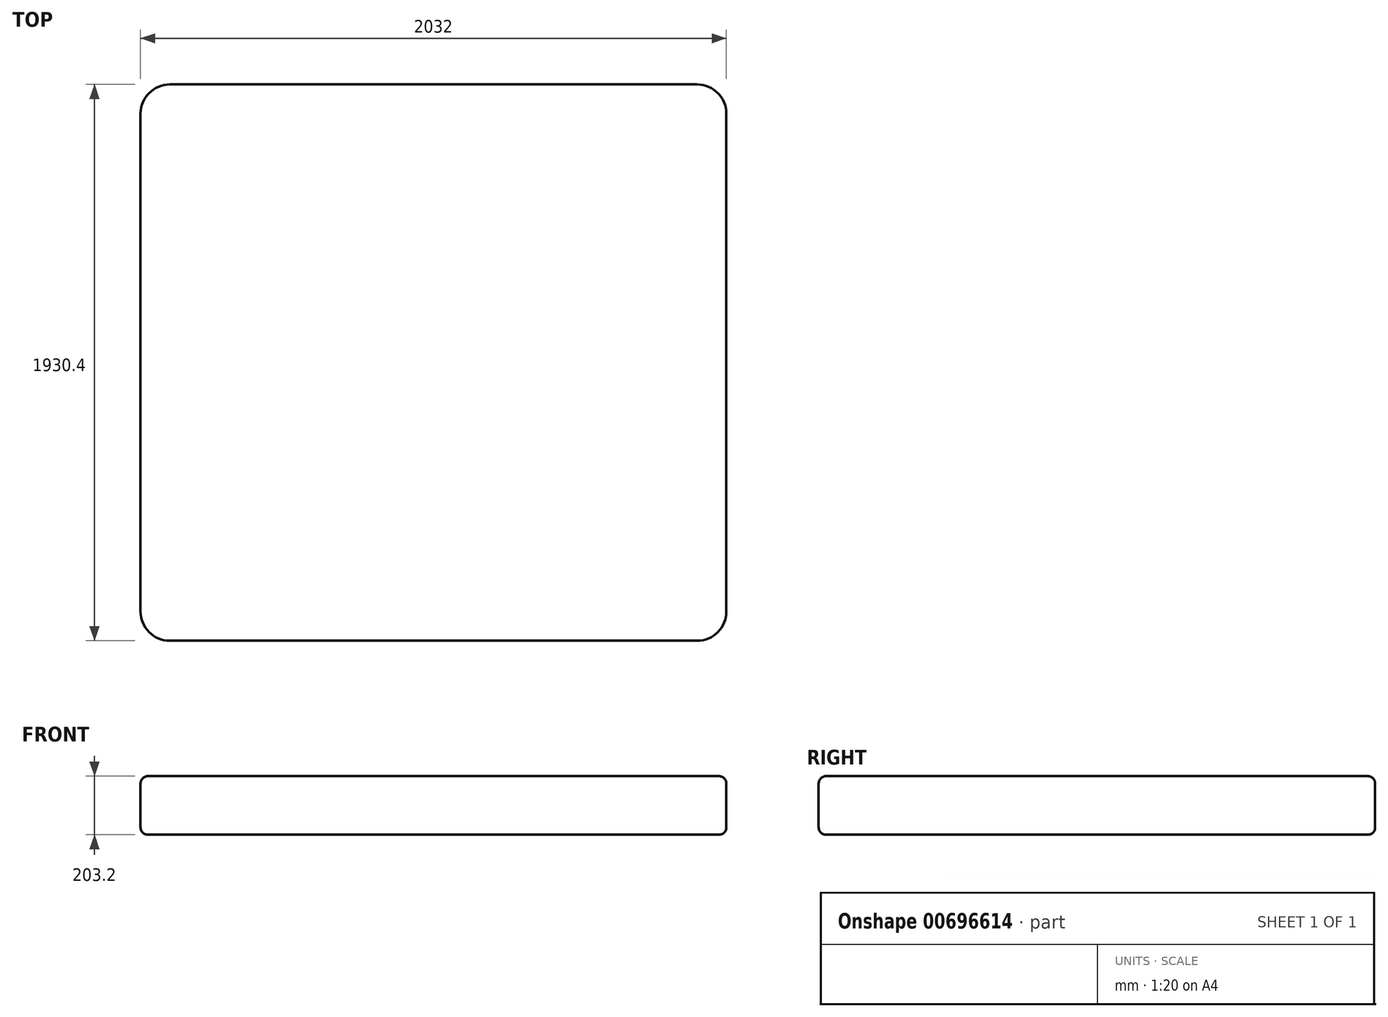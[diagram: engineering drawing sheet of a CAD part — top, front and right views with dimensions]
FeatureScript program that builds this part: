
annotation { "Feature Type Name" : "Feature", "Feature Type Description" : "" }
export const myFeature = defineFeature(function(context is Context, id is Id, definition is map)
    precondition{}
    {
        {
            var Q0;
            Q0=qCreatedBy(makeId("Top.planeOp"),FACE);
            var sketch = newSketch(context, id + "F0", { "sketchPlane" : qUnion([Q0])});
            skLineSegment(sketch, "E0.bottom", {"start": v(0, 0) * mm, "end": v(2032, 0) * mm});
            skLineSegment(sketch, "E0.top", {"start": v(0, 1930.4) * mm, "end": v(2032, 1930.4) * mm});
            skLineSegment(sketch, "E0.left", {"start": v(0, 0) * mm, "end": v(0, 1930.4) * mm});
            skLineSegment(sketch, "E0.right", {"start": v(2032, 0) * mm, "end": v(2032, 1930.4) * mm});
            skSolve(sketch);
        }
        {
            var Q0;
            Q0 = qSketchRegion(id + "F0", true);
            extrude(context, id + "F1", {"entities" : qUnion([Q0]), "depth" : 203.2 * mm, "offsetDistance" : 25.4 * mm});
        }
        {
            var Q0;
            Q0=makeQuery(id+"F1.opExtrude","SWEPT_EDGE",EDGE,{"disambiguationData":[OSD([sQuery(id+"F0.wireOp",EDGE,"E0.top"),sQuery(id+"F0.wireOp",EDGE,"E0.left")])]});
            var Q1;
            Q1=makeQuery(id+"F1.opExtrude","SWEPT_EDGE",EDGE,{"disambiguationData":[OSD([sQuery(id+"F0.wireOp",EDGE,"E0.bottom"),sQuery(id+"F0.wireOp",EDGE,"E0.left")])]});
            var Q2;
            Q2=makeQuery(id+"F1.opExtrude","SWEPT_EDGE",EDGE,{"disambiguationData":[OSD([sQuery(id+"F0.wireOp",EDGE,"E0.bottom"),sQuery(id+"F0.wireOp",EDGE,"E0.right")])]});
            var Q3;
            Q3=makeQuery(id+"F1.opExtrude","SWEPT_EDGE",EDGE,{"disambiguationData":[OSD([sQuery(id+"F0.wireOp",EDGE,"E0.top"),sQuery(id+"F0.wireOp",EDGE,"E0.right")])]});
            fillet(context, id + "F2", {"entities" : qUnion([Q0, Q1, Q2, Q3]), "radius" : 101.6 * mm, "tangentPropagation" : true, "allowEdgeOverflow" : false});
        }
        {
            var Q0;
            Q0=makeQuery(id+"F1.opExtrude","CAP_EDGE",EDGE,{"disambiguationData":[OSD([sQuery(id+"F0.wireOp",EDGE,"E0.top")])],"isStart":false});
            var Q1;
            {var subQ0=sQuery(id+"F0.wireOp",EDGE,"E0.left");var subQ1=sQuery(id+"F0.wireOp",EDGE,"E0.top");Q1=makeQuery(id+"F2.opFillet","BLEND_EDGE",EDGE,{"blendedFrom":[makeQuery(id+"F1.opExtrude","SWEPT_EDGE",EDGE,{"disambiguationData":[OSD([subQ1,subQ0])]}),makeQuery(id+"F1.opExtrude","CAP_FACE",FACE,{"disambiguationData":[OSD([sQuery(id+"F0.wireOp",EDGE,"E0.bottom"),subQ1,subQ0,sQuery(id+"F0.wireOp",EDGE,"E0.right")])],"isStart":false})],"blendedInto":[makeQuery(id+"F1.opExtrude","CAP_FACE",FACE,{"disambiguationData":[OSD([sQuery(id+"F0.wireOp",EDGE,"E0.bottom"),subQ1,subQ0,sQuery(id+"F0.wireOp",EDGE,"E0.right")])],"isStart":false})]});}
            var Q2;
            Q2=makeQuery(id+"F1.opExtrude","CAP_EDGE",EDGE,{"disambiguationData":[OSD([sQuery(id+"F0.wireOp",EDGE,"E0.left")])],"isStart":false});
            var Q3;
            {var subQ0=sQuery(id+"F0.wireOp",EDGE,"E0.left");var subQ1=sQuery(id+"F0.wireOp",EDGE,"E0.bottom");Q3=makeQuery(id+"F2.opFillet","BLEND_EDGE",EDGE,{"blendedFrom":[makeQuery(id+"F1.opExtrude","SWEPT_EDGE",EDGE,{"disambiguationData":[OSD([subQ1,subQ0])]}),makeQuery(id+"F1.opExtrude","CAP_FACE",FACE,{"disambiguationData":[OSD([subQ1,sQuery(id+"F0.wireOp",EDGE,"E0.top"),subQ0,sQuery(id+"F0.wireOp",EDGE,"E0.right")])],"isStart":false})],"blendedInto":[makeQuery(id+"F1.opExtrude","CAP_FACE",FACE,{"disambiguationData":[OSD([subQ1,sQuery(id+"F0.wireOp",EDGE,"E0.top"),subQ0,sQuery(id+"F0.wireOp",EDGE,"E0.right")])],"isStart":false})]});}
            var Q4;
            Q4=makeQuery(id+"F1.opExtrude","CAP_EDGE",EDGE,{"disambiguationData":[OSD([sQuery(id+"F0.wireOp",EDGE,"E0.bottom")])],"isStart":false});
            var Q5;
            {var subQ0=sQuery(id+"F0.wireOp",EDGE,"E0.right");var subQ1=sQuery(id+"F0.wireOp",EDGE,"E0.bottom");Q5=makeQuery(id+"F2.opFillet","BLEND_EDGE",EDGE,{"blendedFrom":[makeQuery(id+"F1.opExtrude","SWEPT_EDGE",EDGE,{"disambiguationData":[OSD([subQ1,subQ0])]}),makeQuery(id+"F1.opExtrude","CAP_FACE",FACE,{"disambiguationData":[OSD([subQ1,sQuery(id+"F0.wireOp",EDGE,"E0.top"),sQuery(id+"F0.wireOp",EDGE,"E0.left"),subQ0])],"isStart":false})],"blendedInto":[makeQuery(id+"F1.opExtrude","CAP_FACE",FACE,{"disambiguationData":[OSD([subQ1,sQuery(id+"F0.wireOp",EDGE,"E0.top"),sQuery(id+"F0.wireOp",EDGE,"E0.left"),subQ0])],"isStart":false})]});}
            var Q6;
            Q6=makeQuery(id+"F1.opExtrude","CAP_EDGE",EDGE,{"disambiguationData":[OSD([sQuery(id+"F0.wireOp",EDGE,"E0.right")])],"isStart":false});
            var Q7;
            {var subQ0=sQuery(id+"F0.wireOp",EDGE,"E0.right");var subQ1=sQuery(id+"F0.wireOp",EDGE,"E0.top");Q7=makeQuery(id+"F2.opFillet","BLEND_EDGE",EDGE,{"blendedFrom":[makeQuery(id+"F1.opExtrude","SWEPT_EDGE",EDGE,{"disambiguationData":[OSD([subQ1,subQ0])]}),makeQuery(id+"F1.opExtrude","CAP_FACE",FACE,{"disambiguationData":[OSD([sQuery(id+"F0.wireOp",EDGE,"E0.bottom"),subQ1,sQuery(id+"F0.wireOp",EDGE,"E0.left"),subQ0])],"isStart":false})],"blendedInto":[makeQuery(id+"F1.opExtrude","CAP_FACE",FACE,{"disambiguationData":[OSD([sQuery(id+"F0.wireOp",EDGE,"E0.bottom"),subQ1,sQuery(id+"F0.wireOp",EDGE,"E0.left"),subQ0])],"isStart":false})]});}
            fillet(context, id + "F3", {"entities" : qUnion([Q0, Q1, Q2, Q3, Q4, Q5, Q6, Q7]), "radius" : 25.4 * mm, "tangentPropagation" : true, "allowEdgeOverflow" : false});
        }
        {
            var Q0;
            {var subQ0=sQuery(id+"F0.wireOp",EDGE,"E0.right");var subQ1=sQuery(id+"F0.wireOp",EDGE,"E0.bottom");Q0=makeQuery(id+"F2.opFillet","BLEND_EDGE",EDGE,{"blendedFrom":[makeQuery(id+"F1.opExtrude","SWEPT_EDGE",EDGE,{"disambiguationData":[OSD([subQ1,subQ0])]}),makeQuery(id+"F1.opExtrude","CAP_FACE",FACE,{"disambiguationData":[OSD([subQ1,sQuery(id+"F0.wireOp",EDGE,"E0.top"),sQuery(id+"F0.wireOp",EDGE,"E0.left"),subQ0])],"isStart":true})],"blendedInto":[makeQuery(id+"F1.opExtrude","CAP_FACE",FACE,{"disambiguationData":[OSD([subQ1,sQuery(id+"F0.wireOp",EDGE,"E0.top"),sQuery(id+"F0.wireOp",EDGE,"E0.left"),subQ0])],"isStart":true})]});}
            var Q1;
            Q1=makeQuery(id+"F1.opExtrude","CAP_EDGE",EDGE,{"disambiguationData":[OSD([sQuery(id+"F0.wireOp",EDGE,"E0.bottom")])],"isStart":true});
            var Q2;
            {var subQ0=sQuery(id+"F0.wireOp",EDGE,"E0.left");var subQ1=sQuery(id+"F0.wireOp",EDGE,"E0.bottom");Q2=makeQuery(id+"F2.opFillet","BLEND_EDGE",EDGE,{"blendedFrom":[makeQuery(id+"F1.opExtrude","SWEPT_EDGE",EDGE,{"disambiguationData":[OSD([subQ1,subQ0])]}),makeQuery(id+"F1.opExtrude","CAP_FACE",FACE,{"disambiguationData":[OSD([subQ1,sQuery(id+"F0.wireOp",EDGE,"E0.top"),subQ0,sQuery(id+"F0.wireOp",EDGE,"E0.right")])],"isStart":true})],"blendedInto":[makeQuery(id+"F1.opExtrude","CAP_FACE",FACE,{"disambiguationData":[OSD([subQ1,sQuery(id+"F0.wireOp",EDGE,"E0.top"),subQ0,sQuery(id+"F0.wireOp",EDGE,"E0.right")])],"isStart":true})]});}
            var Q3;
            Q3=makeQuery(id+"F1.opExtrude","CAP_EDGE",EDGE,{"disambiguationData":[OSD([sQuery(id+"F0.wireOp",EDGE,"E0.left")])],"isStart":true});
            var Q4;
            {var subQ0=sQuery(id+"F0.wireOp",EDGE,"E0.left");var subQ1=sQuery(id+"F0.wireOp",EDGE,"E0.top");Q4=makeQuery(id+"F2.opFillet","BLEND_EDGE",EDGE,{"blendedFrom":[makeQuery(id+"F1.opExtrude","SWEPT_EDGE",EDGE,{"disambiguationData":[OSD([subQ1,subQ0])]}),makeQuery(id+"F1.opExtrude","CAP_FACE",FACE,{"disambiguationData":[OSD([sQuery(id+"F0.wireOp",EDGE,"E0.bottom"),subQ1,subQ0,sQuery(id+"F0.wireOp",EDGE,"E0.right")])],"isStart":true})],"blendedInto":[makeQuery(id+"F1.opExtrude","CAP_FACE",FACE,{"disambiguationData":[OSD([sQuery(id+"F0.wireOp",EDGE,"E0.bottom"),subQ1,subQ0,sQuery(id+"F0.wireOp",EDGE,"E0.right")])],"isStart":true})]});}
            var Q5;
            Q5=makeQuery(id+"F1.opExtrude","CAP_EDGE",EDGE,{"disambiguationData":[OSD([sQuery(id+"F0.wireOp",EDGE,"E0.top")])],"isStart":true});
            var Q6;
            {var subQ0=sQuery(id+"F0.wireOp",EDGE,"E0.right");var subQ1=sQuery(id+"F0.wireOp",EDGE,"E0.top");Q6=makeQuery(id+"F2.opFillet","BLEND_EDGE",EDGE,{"blendedFrom":[makeQuery(id+"F1.opExtrude","SWEPT_EDGE",EDGE,{"disambiguationData":[OSD([subQ1,subQ0])]}),makeQuery(id+"F1.opExtrude","CAP_FACE",FACE,{"disambiguationData":[OSD([sQuery(id+"F0.wireOp",EDGE,"E0.bottom"),subQ1,sQuery(id+"F0.wireOp",EDGE,"E0.left"),subQ0])],"isStart":true})],"blendedInto":[makeQuery(id+"F1.opExtrude","CAP_FACE",FACE,{"disambiguationData":[OSD([sQuery(id+"F0.wireOp",EDGE,"E0.bottom"),subQ1,sQuery(id+"F0.wireOp",EDGE,"E0.left"),subQ0])],"isStart":true})]});}
            var Q7;
            Q7=makeQuery(id+"F1.opExtrude","CAP_EDGE",EDGE,{"disambiguationData":[OSD([sQuery(id+"F0.wireOp",EDGE,"E0.right")])],"isStart":true});
            fillet(context, id + "F4", {"entities" : qUnion([Q0, Q1, Q2, Q3, Q4, Q5, Q6, Q7]), "radius" : 25.4 * mm, "tangentPropagation" : true, "allowEdgeOverflow" : false});
        }
    });
